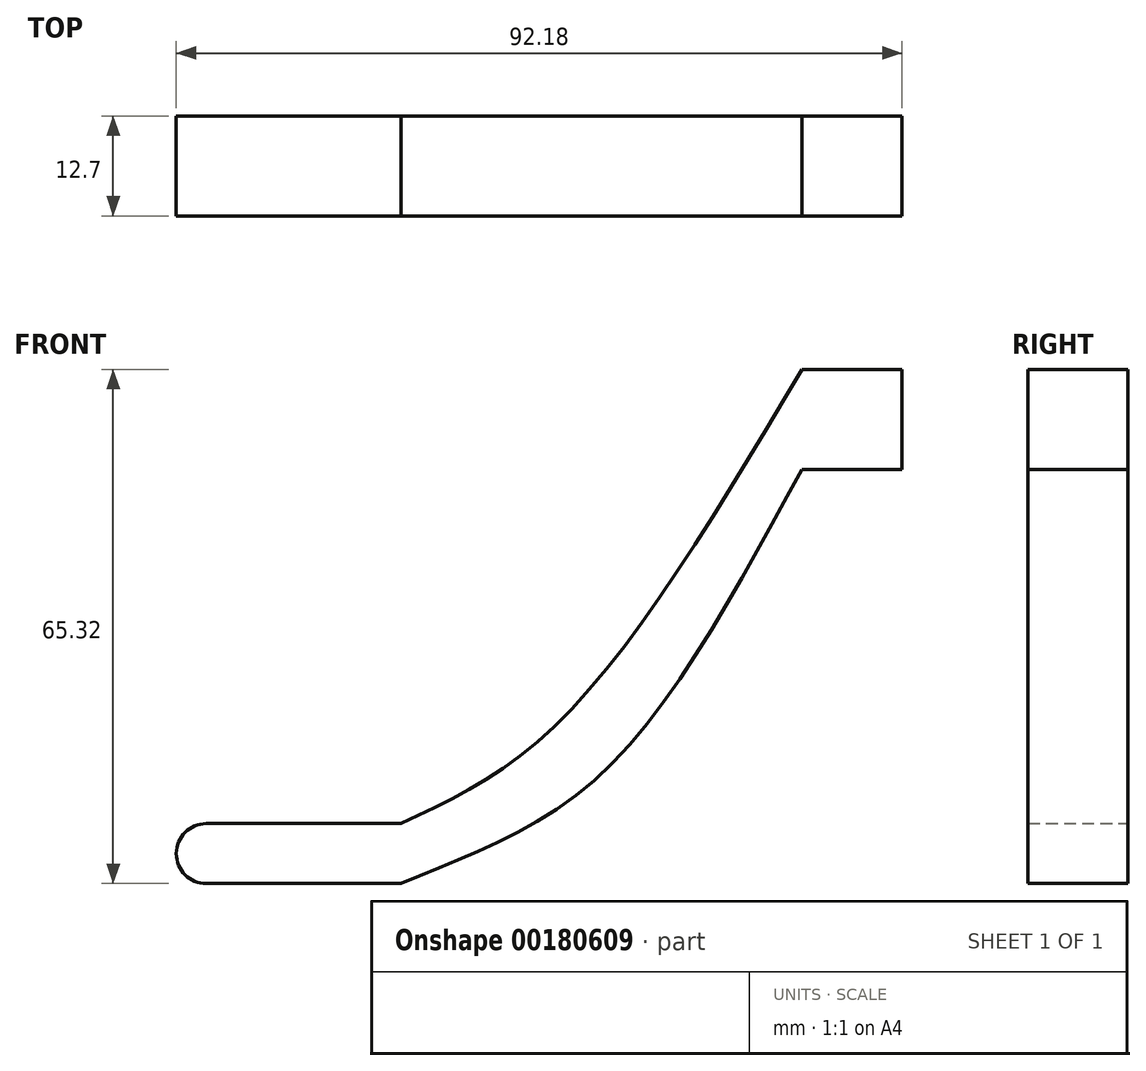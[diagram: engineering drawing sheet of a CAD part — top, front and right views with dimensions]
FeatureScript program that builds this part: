
annotation { "Feature Type Name" : "Feature", "Feature Type Description" : "" }
export const myFeature = defineFeature(function(context is Context, id is Id, definition is map)
    precondition{}
    {
        {
            var Q0;
            Q0=qCreatedBy(makeId("Front.planeOp"),FACE);
            var sketch = newSketch(context, id + "F0", { "sketchPlane" : qUnion([Q0])});
            skCircle(sketch, "E0.cCircle", {"center": v(18.54, 58.97) * mm, "radius": 6.35 * mm, "construction": true});
            skLineSegment(sketch, "E0.0", {"start": v(24.9, 65.32) * mm, "end": v(24.9, 52.62) * mm});
            skLineSegment(sketch, "E0.1", {"start": v(24.9, 52.62) * mm, "end": v(12.2, 52.62) * mm});
            skLineSegment(sketch, "E0.2", {"start": v(12.2, 52.62) * mm, "end": v(12.2, 65.32) * mm});
            skLineSegment(sketch, "E0.3", {"start": v(12.2, 65.32) * mm, "end": v(24.9, 65.32) * mm});
            skPoint(sketch, "E0.0.midPoint", {"position": v(24.9, 58.97) * mm});
            skLineSegment(sketch, "E1", {"start": v(12.2, 52.62) * mm, "end": v(12.2, 0) * mm});
            skFitSpline(sketch, "E2", {"points": [v(12.2, 52.62) * mm, v(-14.3, 13.02) * mm, v(-38.72, 0) * mm], "startDerivative": vector(-44.12, -79.52) * mm, "endDerivative": vector(-53.3, -22.8) * mm});
            skLineSegment(sketch, "E3.bottom", {"start": v(-38.72, 0) * mm, "end": v(-63.48, 0) * mm});
            skLineSegment(sketch, "E3.top", {"start": v(-38.72, 7.62) * mm, "end": v(-63.48, 7.62) * mm});
            skFitSpline(sketch, "E4", {"points": [v(12.2, 65.32) * mm, v(-19.11, 20.1) * mm, v(-38.72, 7.62) * mm], "startDerivative": vector(-52.23, -87.6) * mm, "endDerivative": vector(-49.39, -23.25) * mm});
            skArc(sketch, "E5", {"start": v(-63.48, 7.62) * mm, "mid": v(-67.3, 3.81) * mm, "end": v(-63.48, 0) * mm});
            skSolve(sketch);
        }
        {
            var Q0;
            Q0 = qSketchRegion(id + "F0", true);
            extrude(context, id + "F1", {"entities" : qUnion([Q0]), "depth" : 12.7 * mm});
        }
        {
            var Q0;
            Q0 = qSketchRegion(id + "F0", true);
            extrude(context, id + "F2", {"entities" : qUnion([Q0]), "operationType" : NewBodyOperationType.ADD, "depth" : 12.7 * mm});
        }
    });
